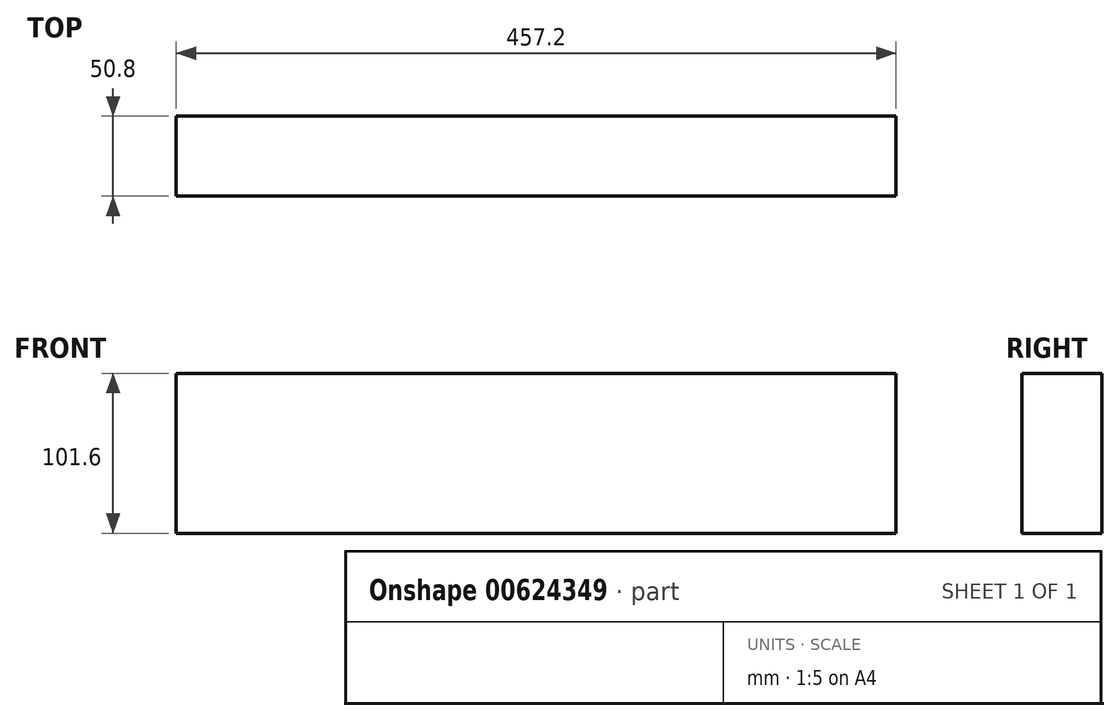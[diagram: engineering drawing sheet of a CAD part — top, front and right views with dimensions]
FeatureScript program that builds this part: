
annotation { "Feature Type Name" : "Feature", "Feature Type Description" : "" }
export const myFeature = defineFeature(function(context is Context, id is Id, definition is map)
    precondition{}
    {
        {
            var Q0;
            Q0=qCreatedBy(makeId("Front.planeOp"),FACE);
            var sketch = newSketch(context, id + "F0", { "sketchPlane" : qUnion([Q0])});
            skLineSegment(sketch, "E0.bottom", {"start": v(-228.6, -50.8) * mm, "end": v(228.6, -50.8) * mm});
            skLineSegment(sketch, "E0.top", {"start": v(-228.6, 50.8) * mm, "end": v(228.6, 50.8) * mm});
            skLineSegment(sketch, "E0.left", {"start": v(-228.6, -50.8) * mm, "end": v(-228.6, 50.8) * mm});
            skLineSegment(sketch, "E0.right", {"start": v(228.6, -50.8) * mm, "end": v(228.6, 50.8) * mm});
            skPoint(sketch, "E0.middle", {"position": v(0, 0) * mm});
            skSolve(sketch);
        }
        {
            var Q0;
            Q0=makeQuery(id+"F0.imprint","IMPRINT",FACE,{"disambiguationData":[TD([[makeQuery(id+"F0.imprint","IMPRINT",EDGE,{"derivedFrom":sQuery(id+"F0.wireOp",EDGE,"E0.bottom")}),1.0]])]});
            extrude(context, id + "F1", {"entities" : qUnion([Q0]), "depth" : 50.8 * mm, "offsetDistance" : 25.4 * mm});
        }
    });
